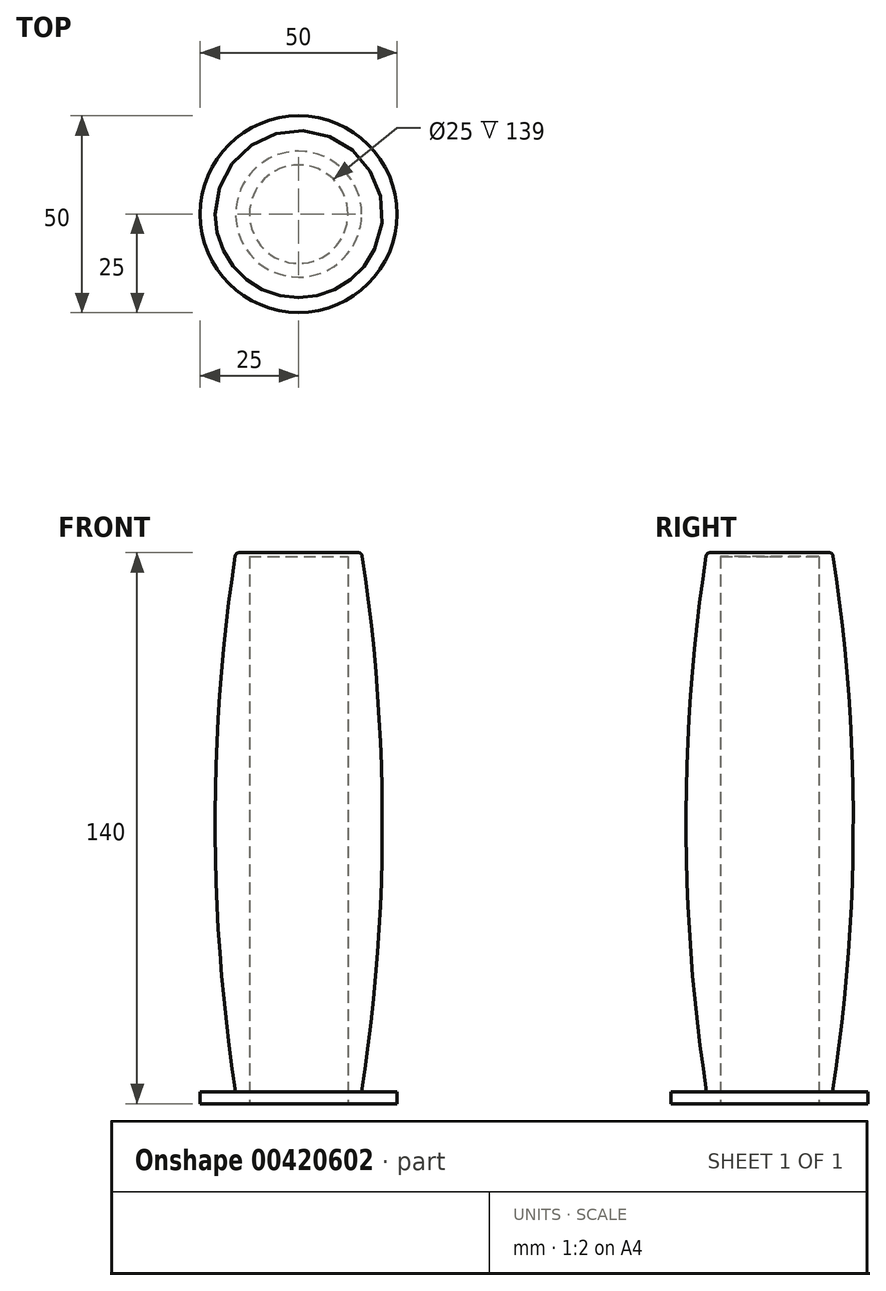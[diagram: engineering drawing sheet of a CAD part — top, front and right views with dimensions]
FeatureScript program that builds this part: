
annotation { "Feature Type Name" : "Feature", "Feature Type Description" : "" }
export const myFeature = defineFeature(function(context is Context, id is Id, definition is map)
    precondition{}
    {
        {
            var Q0;
            Q0=qCreatedBy(makeId("Front.planeOp"),FACE);
            var sketch = newSketch(context, id + "F0", { "sketchPlane" : qUnion([Q0])});
            skLineSegment(sketch, "E0", {"start": v(0, 0) * mm, "end": v(0, 69.73) * mm, "construction": true});
            skLineSegment(sketch, "E1", {"start": v(-25, 0) * mm, "end": v(-25, 3) * mm});
            skLineSegment(sketch, "E2", {"start": v(-25, 3) * mm, "end": v(-16, 3) * mm});
            skLineSegment(sketch, "E3", {"start": v(-12.5, 140) * mm, "end": v(-12.5, 0) * mm, "construction": true});
            skLineSegment(sketch, "E4", {"start": v(-12.5, 0) * mm, "end": v(-25, 0) * mm});
            skLineSegment(sketch, "E5", {"start": v(-16, 3) * mm, "end": v(-16, 140) * mm, "construction": true});
            skLineSegment(sketch, "E6", {"start": v(-12.5, 140) * mm, "end": v(-16, 140) * mm});
            skArc(sketch, "E7", {"start": v(-16, 140) * mm, "mid": v(-21.24, 71.5) * mm, "end": v(-16, 3) * mm});
            skLineSegment(sketch, "E8", {"start": v(-12.5, 140) * mm, "end": v(0, 140) * mm});
            skLineSegment(sketch, "E9", {"start": v(0, 140) * mm, "end": v(0, 139) * mm});
            skLineSegment(sketch, "E10", {"start": v(0, 139) * mm, "end": v(-12.5, 139) * mm});
            skLineSegment(sketch, "E11", {"start": v(-12.5, 139) * mm, "end": v(-12.5, 0) * mm});
            skSolve(sketch);
        }
        {
            var Q0;
            Q0=qSketchRegion(id+"F0",true);
            var Q1;
            Q1=sQuery(id+"F0.wireOp",EDGE,"E0");
            revolve(context, id + "F1", {"entities" : qUnion([Q0]), "axis" : qUnion([Q1]), "revolveType" : RevolveType.FULL});
        }
        {
            var Q0;
            Q0=makeQuery(id+"F1.opRevolve","SWEPT_EDGE",EDGE,{"disambiguationData":[OSD([sQuery(id+"F0.wireOp",EDGE,"E5"),sQuery(id+"F0.wireOp",EDGE,"E6")])]});
            var Q1;
            Q1=makeQuery(id+"F1.opRevolve","SWEPT_EDGE",EDGE,{"disambiguationData":[OSD([sQuery(id+"F0.wireOp",EDGE,"E3"),sQuery(id+"F0.wireOp",EDGE,"E6")])]});
            fillet(context, id + "F2", {"entities" : qUnion([Q0, Q1]), "radius" : 1 * mm, "tangentPropagation" : true, "allowEdgeOverflow" : false});
        }
    });
